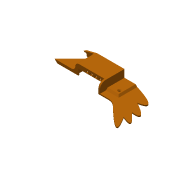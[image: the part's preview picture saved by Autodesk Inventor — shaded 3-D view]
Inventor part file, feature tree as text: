
AUTODESK INVENTOR PART (.ipt)
format: ipt  version: 2016 (Build 200138000, 138)  size: 191,488 bytes
history: native  units: in
note: dims shown in document units (in); Inventor stores cm internally (conversion verified against a paired STEP export)
features: other x3, reference x2, chamfer x1, extrude x1, sketch x1
ambient origin geometry x8: Origin, YZ Plane, XZ Plane, XY Plane, X Axis, Y Axis, Z Axis, Center Point
bodies: Solid1 (feature_tree)
feature tree (8):
  other  "P_ankle02_001.ipt"
  chamfer  "Chamfer1"  Distance=0.0591in Angle=45.0deg
  extrude  "Extrusion1"  Depth=0.3937in TaperAngle=0.0deg
  other  "Solid1::P_ankle02_001.ipt"
  other  "TaggingFeature1"
  sketch  "Sketch1"  dims[d0=0.3937in d1=0.0591in d2=0.125in d3=45.0deg d4=0.3937in d5=0.0in]
  reference  "Reference1"
  reference  "Reference2"
